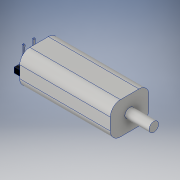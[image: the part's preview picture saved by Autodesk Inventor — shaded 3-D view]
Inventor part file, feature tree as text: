
AUTODESK INVENTOR PART (.ipt)
format: ipt  version: 2018 (Build 220112000, 112)  size: 211,968 bytes
history: native  units: in
note: dims shown in document units (in); Inventor stores cm internally (conversion verified against a paired STEP export)
features: sketch x5, extrude x3, fillet x1, sweep x1, plane x1, chamfer x1
ambient origin geometry x8: Origin, YZ Plane, XZ Plane, XY Plane, X Axis, Y Axis, Z Axis, Center Point
bodies: Solid1 (feature_tree)
feature tree (12):
  extrude  "Extrusion1"  Depth=0.48in
  fillet  "Fillet1"  Radius=1.125in
  extrude  "Extrusion2"  Depth=0.118in
  sweep  "Sweep1"
  plane  "Work Plane1"
  extrude  "Extrusion3"  TaperAngle=0.0deg  [1 undecoded]
  chamfer  "Chamfer1"  Distance=0.07in
  sketch  "Sketch1"  dims[d0=0.4in d1=0.48in d2=1.125in d3=0.0in]
  sketch  "Sketch2"  dims[d4=0.125in d5=0.118in]
  sketch  "Sketch3"  dims[d6=0.3in d7=0.0in d8=0.02in]
  sketch  "Sketch4"  dims[d9=0.015in d10=0.0in d11=0.0in]
  sketch  "Sketch5"  dims[d12=0.125in d13=0.07in d14=0.0in d15=0.006in d16=0.125in d17=45.0deg]
note: 1 required parameter value undecoded (feature->parameter linkage not recoverable at this tier; creation-order binding heuristic only, values carry confidence <= 0.55)
